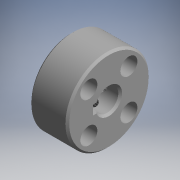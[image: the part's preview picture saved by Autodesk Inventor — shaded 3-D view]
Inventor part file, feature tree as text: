
AUTODESK INVENTOR PART (.ipt)
format: ipt  version: 2017.3 (Build 213256000, 256)  size: 161,792 bytes
history: native  units: mm (DEFAULTED — no unit token found)
features: sketch x8, other x7, extrude x5, revolve x3, thread x2
ambient origin geometry x8: Origin, YZ Plane, XZ Plane, XY Plane, X Axis, Y Axis, Z Axis, Center Point
bodies: Solid1 (feature_tree)
feature tree (25):
  revolve  "Revolution1"  Angle=360.0deg
  revolve  "Revolution2"  Angle=360.0deg
  thread  "Thread1"  [1 undecoded]
  revolve  "Revolution3"  [1 undecoded]
  thread  "Thread2"  [1 undecoded]
  extrude  "Extrusion1"  Depth=10.0mm TaperAngle=0.0deg
  extrude  "Extrusion2"  [1 undecoded]
  extrude  "Extrusion3"  [1 undecoded]
  extrude  "Extrusion4"  [1 undecoded]
  extrude  "Extrusion5"  [1 undecoded]
  other  "part_XY"
  other  "part_YZ"
  other  "part_ZX"
  other  "part_X"
  other  "part_Y"
  other  "part_Z"
  other  "part_Center"
  sketch  "Sketch_1"  dims[d0=360.0deg d1=360.0deg]
  sketch  "Sketch_4"  dims[d13=10.0mm d14=0.0mm d15=10.0mm d16=0.0mm]
  sketch  "Sketch_3"  dims[d7=10.0mm d8=0.0mm d9=10.0mm d10=0.0mm d11=10.0mm d12=0.0mm]
  sketch  "Sketch_2"  dims[d2=7.621mm d3=0.0mm d4=360.0deg d5=7.621mm d6=0.0mm]
  sketch  "Sketch_6"  dims[d17=0.0mm]
  sketch  "Sketch_7"
  sketch  "Sketch_8"
  sketch  "Sketch_9"
note: 7 required parameter values undecoded (feature->parameter linkage not recoverable at this tier; creation-order binding heuristic only, values carry confidence <= 0.55)